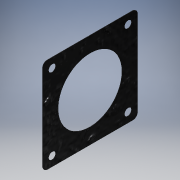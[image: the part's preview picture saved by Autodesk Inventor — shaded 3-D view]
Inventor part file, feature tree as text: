
AUTODESK INVENTOR PART (.ipt)
format: ipt  version: 2018 (Build 220112000, 112)  size: 128,512 bytes
history: native  units: mm
features: extrude x1, sketch x1
ambient origin geometry x8: Origin, YZ Plane, XZ Plane, XY Plane, X Axis, Y Axis, Z Axis, Center Point
bodies: Solid1 (feature_tree)
feature tree (2):
  extrude  "Extrusion1"  Depth=40.0mm
  sketch  "Sketch1"  dims[d0=40.0mm d1=40.0mm d2=3.0mm d3=27.0mm d4=32.0mm d5=32.0mm d6=2.0mm d7=0.2mm d8=0.0mm]
